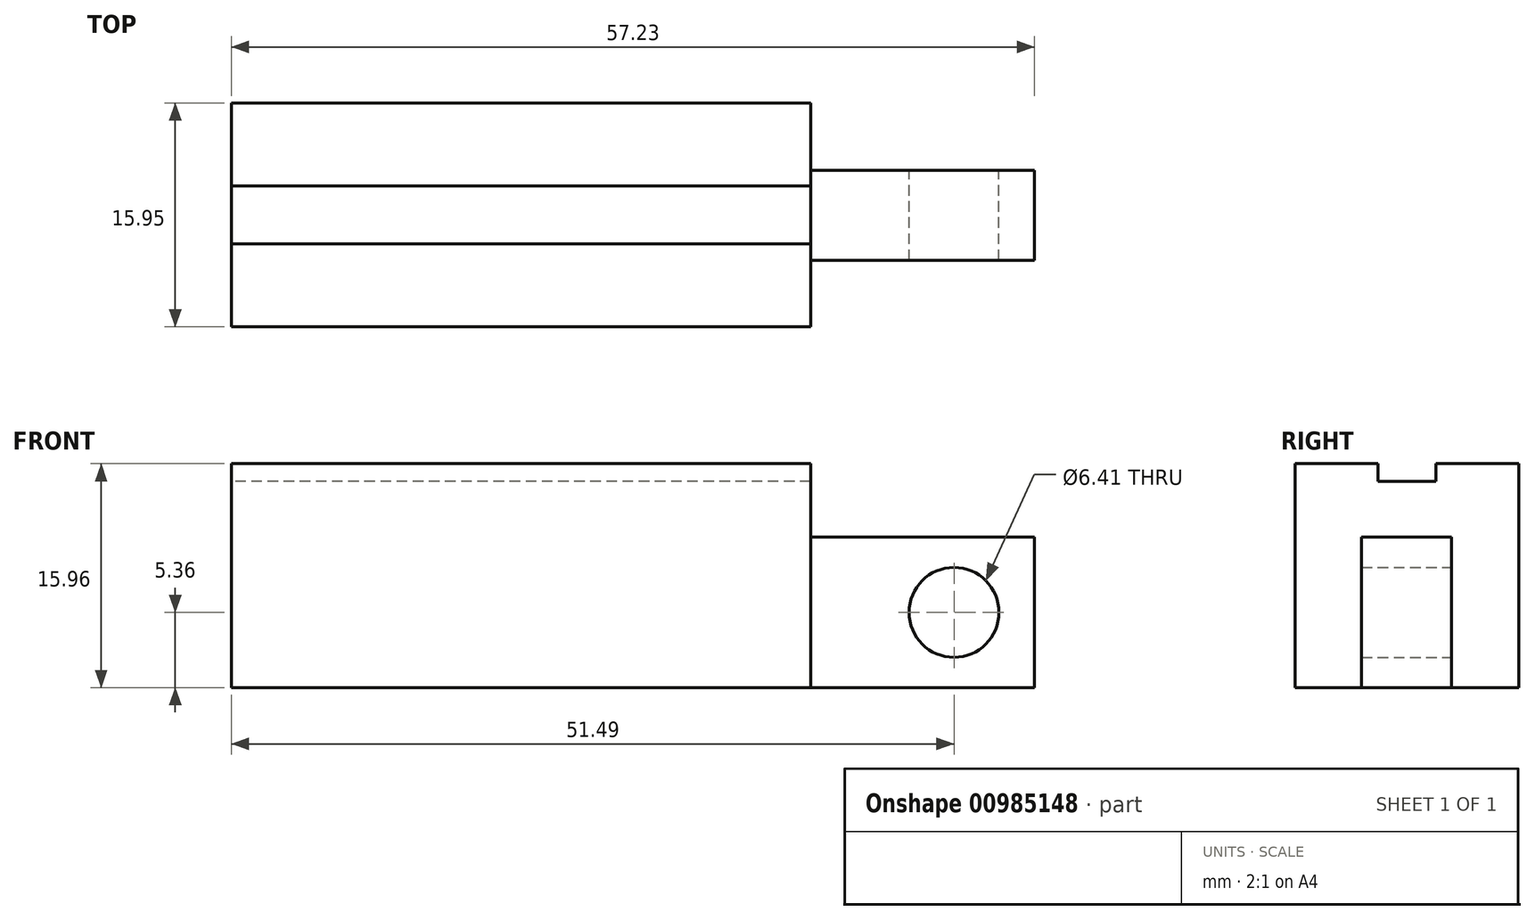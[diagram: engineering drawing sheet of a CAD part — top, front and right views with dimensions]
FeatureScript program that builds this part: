
annotation { "Feature Type Name" : "Feature", "Feature Type Description" : "" }
export const myFeature = defineFeature(function(context is Context, id is Id, definition is map)
    precondition{}
    {
        {
            var Q0;
            Q0=qCreatedBy(makeId("Front.planeOp"),FACE);
            var sketch = newSketch(context, id + "F0", { "sketchPlane" : qUnion([Q0])});
            skLineSegment(sketch, "E0.bottom", {"start": v(-20.64, 7.98) * mm, "end": v(20.64, 7.98) * mm});
            skLineSegment(sketch, "E0.top", {"start": v(-20.64, -7.98) * mm, "end": v(20.64, -7.98) * mm});
            skLineSegment(sketch, "E0.left", {"start": v(-20.64, 7.98) * mm, "end": v(-20.64, -7.98) * mm});
            skLineSegment(sketch, "E0.right", {"start": v(20.64, 7.98) * mm, "end": v(20.64, -7.98) * mm});
            skPoint(sketch, "E0.middle", {"position": v(0, 0) * mm});
            skSolve(sketch);
        }
        {
            var Q0;
            Q0 = qSketchRegion(id + "F0", true);
            extrude(context, id + "F1", {"entities" : qUnion([Q0]), "depth" : 15.95 * mm, "offsetDistance" : 25.4 * mm});
        }
        {
            var Q0;
            Q0=qCreatedBy(makeId("Top.planeOp"),FACE);
            var Q1;
            Q1 = qBodyType(qCreatedBy(id + "F3" ,EDGE), BodyType.WIRE);
            cPlane(context, id + "F2", {"entities" : qUnion([Q0, Q1]), "cplaneType" : CPlaneType.OFFSET, "offset" : 25.4 * mm, "width" : 152.4 * mm, "height" : 152.4 * mm});
        }
        {
            var Q0;
            Q0=qCreatedBy(id+"F2.planeOp",FACE);
            var sketch = newSketch(context, id + "F3", { "sketchPlane" : qUnion([Q0])});
            skLineSegment(sketch, "E1", {"start": v(-28.82, 0) * mm, "end": v(28.8, 0) * mm, "construction": true});
            skLineSegment(sketch, "E2", {"start": v(-12.52, 0) * mm, "end": v(-12.52, -7.98) * mm, "construction": true});
            skLineSegment(sketch, "E3.bottom", {"start": v(20.84, -10.03) * mm, "end": v(-61.8, -10.03) * mm});
            skLineSegment(sketch, "E3.top", {"start": v(20.84, -5.92) * mm, "end": v(-61.8, -5.92) * mm});
            skLineSegment(sketch, "E3.left", {"start": v(20.84, -10.03) * mm, "end": v(20.84, -5.92) * mm});
            skLineSegment(sketch, "E3.right", {"start": v(-61.8, -10.03) * mm, "end": v(-61.8, -5.92) * mm});
            skPoint(sketch, "E3.middle", {"position": v(-20.48, -7.98) * mm});
            skSolve(sketch);
        }
        {
            var Q0;
            Q0=makeQuery(id+"F3.imprint","IMPRINT",FACE,{"disambiguationData":[TD([[makeQuery(id+"F3.imprint","IMPRINT",EDGE,{"derivedFrom":sQuery(id+"F3.wireOp",EDGE,"E3.bottom")}),-1.0]])]});
            extrude(context, id + "F4", {"entities" : qUnion([Q0]), "operationType" : NewBodyOperationType.REMOVE, "oppositeDirection" : true, "depth" : 18.7 * mm, "offsetDistance" : 25.4 * mm});
        }
        {
            var Q0;
            Q0=qCreatedBy(makeId("Right.planeOp"),FACE);
            cPlane(context, id + "F5", {"entities" : qUnion([Q0]), "cplaneType" : CPlaneType.OFFSET, "offset" : 20.64 * mm, "width" : 152.4 * mm, "height" : 152.4 * mm});
        }
        {
            var Q0;
            Q0=qCreatedBy(id+"F5.planeOp",FACE);
            var sketch = newSketch(context, id + "F6", { "sketchPlane" : qUnion([Q0])});
            skLineSegment(sketch, "E4", {"start": v(0, 0) * mm, "end": v(-7.98, 0) * mm, "construction": true});
            skLineSegment(sketch, "E5", {"start": v(0, 0) * mm, "end": v(0, -10.9) * mm, "construction": true});
            skLineSegment(sketch, "E6", {"start": v(-7.98, 0) * mm, "end": v(-7.98, -10.28) * mm, "construction": true});
            skLineSegment(sketch, "E7", {"start": v(0, 2.74) * mm, "end": v(-4.8, 2.74) * mm});
            skLineSegment(sketch, "E8.bottom", {"start": v(-4.8, 2.74) * mm, "end": v(-11.2, 2.74) * mm});
            skLineSegment(sketch, "E8.top", {"start": v(-4.8, -7.98) * mm, "end": v(-11.2, -7.98) * mm});
            skLineSegment(sketch, "E8.left", {"start": v(-4.8, 2.74) * mm, "end": v(-4.8, -7.98) * mm});
            skLineSegment(sketch, "E8.right", {"start": v(-11.2, 2.74) * mm, "end": v(-11.2, -7.98) * mm});
            skSolve(sketch);
        }
        {
            var Q0;
            Q0=makeQuery(id+"F6.imprint","IMPRINT",FACE,{"disambiguationData":[TD([[makeQuery(id+"F6.imprint","IMPRINT",EDGE,{"derivedFrom":sQuery(id+"F6.wireOp",EDGE,"E8.bottom")}),1.0]])]});
            extrude(context, id + "F7", {"entities" : qUnion([Q0]), "operationType" : NewBodyOperationType.ADD, "depth" : 15.95 * mm, "offsetDistance" : 25.4 * mm});
        }
        {
            var Q0;
            Q0=qCreatedBy(makeId("Front.planeOp"),FACE);
            var sketch = newSketch(context, id + "F8", { "sketchPlane" : qUnion([Q0])});
            skCircle(sketch, "E9", {"center": v(30.85, -2.62) * mm, "radius": 3.2 * mm});
            skSolve(sketch);
        }
        {
            var Q0;
            Q0 = qSketchRegion(id + "F8", true);
            extrude(context, id + "F9", {"entities" : qUnion([Q0]), "operationType" : NewBodyOperationType.REMOVE, "depth" : 25.4 * mm, "offsetDistance" : 25.4 * mm});
        }
        {
            var Q0;
            Q0=qCreatedBy(makeId("Front.planeOp"),FACE);
            cPlane(context, id + "F10", {"entities" : qUnion([Q0]), "cplaneType" : CPlaneType.OFFSET, "offset" : 25.4 * mm, "width" : 152.4 * mm, "height" : 152.4 * mm});
        }
    });
